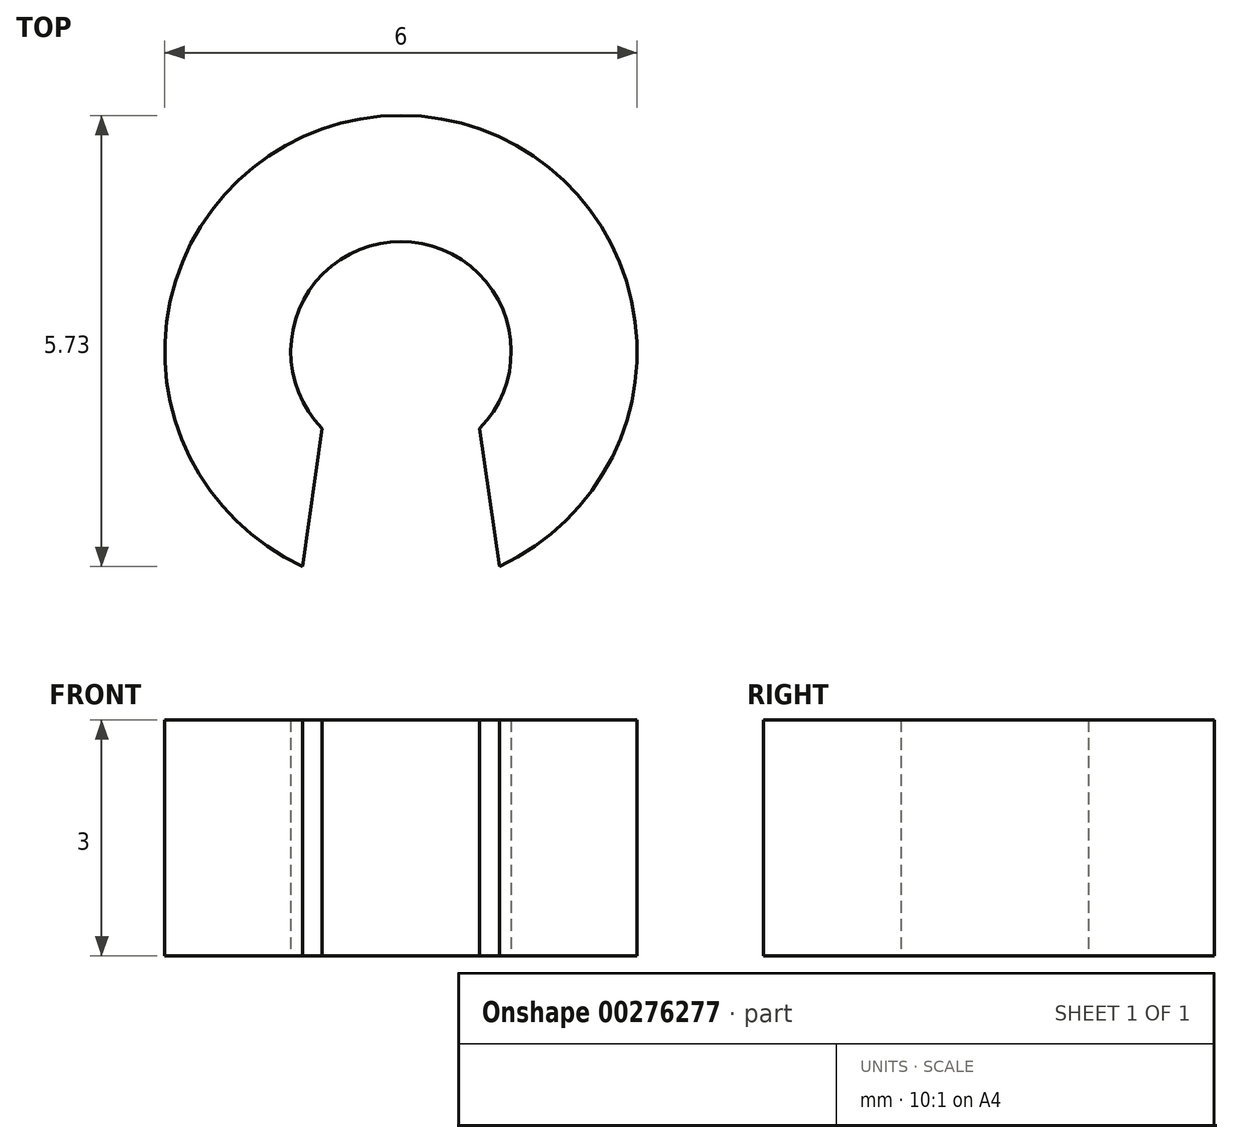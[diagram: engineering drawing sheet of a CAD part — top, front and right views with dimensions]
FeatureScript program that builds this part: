
annotation { "Feature Type Name" : "Feature", "Feature Type Description" : "" }
export const myFeature = defineFeature(function(context is Context, id is Id, definition is map)
    precondition{}
    {
        {
            var Q0;
            Q0=qCreatedBy(makeId("Top.planeOp"),FACE);
            var sketch = newSketch(context, id + "F0", { "sketchPlane" : qUnion([Q0])});
            skArc(sketch, "E0", {"start": v(1.25, -2.73) * mm, "mid": v(0, 3) * mm, "end": v(-1.25, -2.73) * mm});
            skArc(sketch, "E1", {"start": v(1, -0.98) * mm, "mid": v(0, 1.4) * mm, "end": v(-1, -0.98) * mm});
            skLineSegment(sketch, "E2", {"start": v(0, 0) * mm, "end": v(0, -3) * mm, "construction": true});
            skLineSegment(sketch, "E3", {"start": v(1, -0.98) * mm, "end": v(1.25, -2.73) * mm});
            skLineSegment(sketch, "E4", {"start": v(-1, -0.98) * mm, "end": v(-1.25, -2.73) * mm});
            skSolve(sketch);
        }
        {
            var Q0;
            {var subQ0=sQuery(id+"F0.wireOp",EDGE,"E0");Q0=makeQuery(id+"F0.imprint","IMPRINT",FACE,{"disambiguationData":[TD([[makeQuery(id+"F0.imprint","IMPRINT",EDGE,{"derivedFrom":subQ0}),1.0]])]});}
            extrude(context, id + "F1", {"entities" : qUnion([Q0]), "depth" : 3 * mm});
        }
    });
